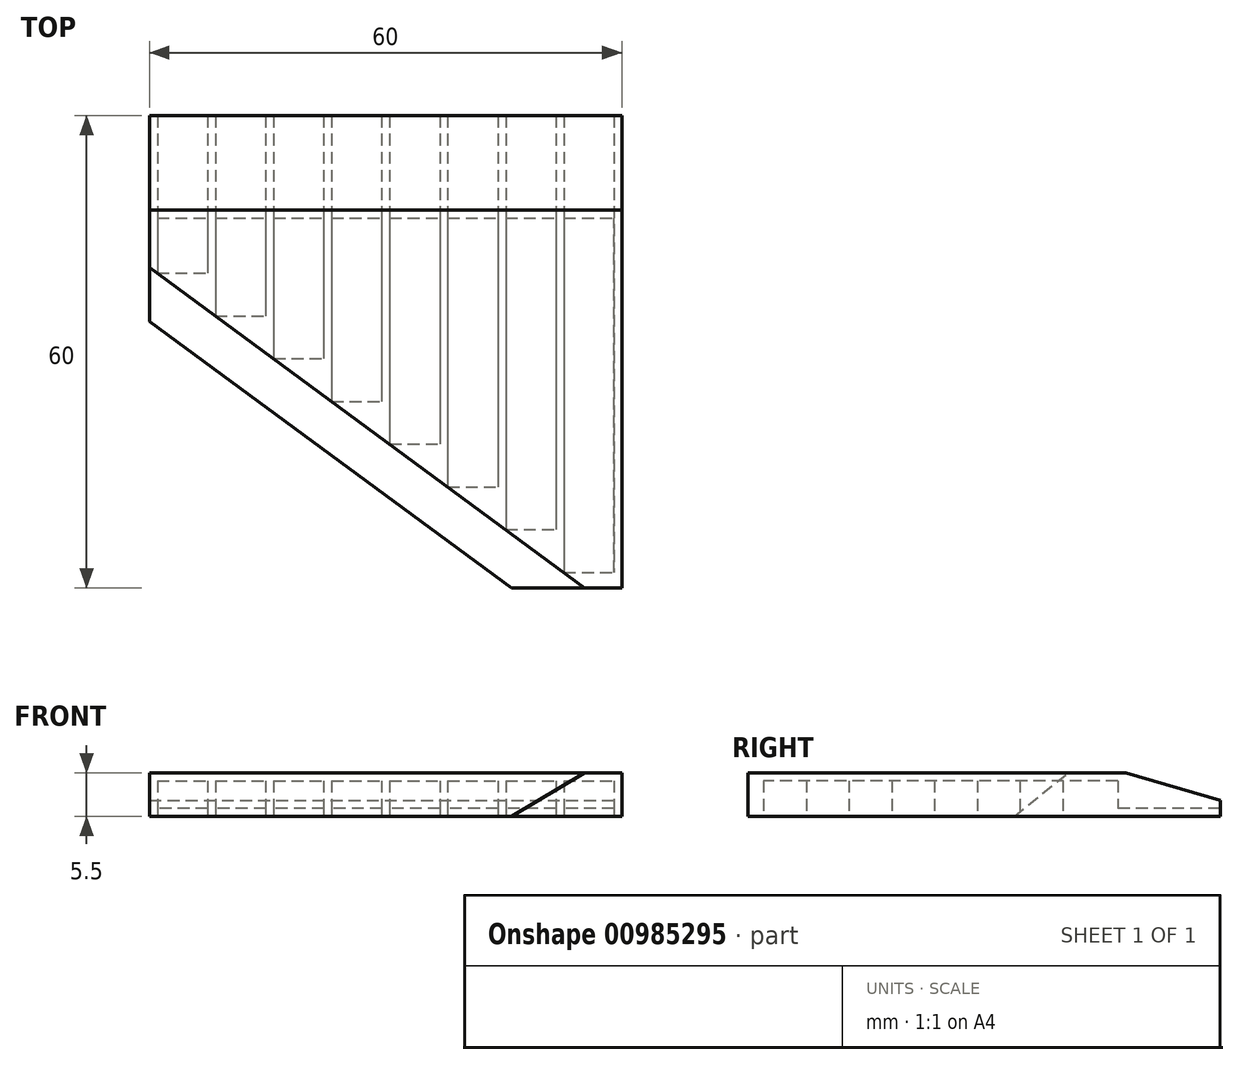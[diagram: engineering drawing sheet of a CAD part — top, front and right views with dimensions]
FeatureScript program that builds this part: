
annotation { "Feature Type Name" : "Feature", "Feature Type Description" : "" }
export const myFeature = defineFeature(function(context is Context, id is Id, definition is map)
    precondition{}
    {
        {
            var Q0;
            Q0=qCreatedBy(makeId("Top.planeOp"),FACE);
            var sketch = newSketch(context, id + "F0", { "sketchPlane" : qUnion([Q0])});
            skLineSegment(sketch, "E0.bottom", {"start": v(30, 30) * mm, "end": v(-30, 30) * mm});
            skLineSegment(sketch, "E0.top", {"start": v(30, -30) * mm, "end": v(-30, -30) * mm});
            skLineSegment(sketch, "E0.left", {"start": v(30, 30) * mm, "end": v(30, -30) * mm});
            skLineSegment(sketch, "E0.right", {"start": v(-30, 30) * mm, "end": v(-30, -30) * mm});
            skPoint(sketch, "E0.middle", {"position": v(0, 0) * mm});
            skSolve(sketch);
        }
        {
            var Q0;
            Q0=makeQuery(id+"F0.imprint","IMPRINT",FACE,{"disambiguationData":[TD([[makeQuery(id+"F0.imprint","IMPRINT",EDGE,{"derivedFrom":sQuery(id+"F0.wireOp",EDGE,"E0.bottom")}),1.0]])]});
            extrude(context, id + "F1", {"entities" : qUnion([Q0]), "depth" : 5.5 * mm, "offsetDistance" : 25 * mm});
        }
        {
            var Q0;
            Q0=makeQuery(id+"F1.opExtrude","SWEPT_FACE",FACE,{"disambiguationData":[OSD([sQuery(id+"F0.wireOp",EDGE,"E0.left")])]});
            var sketch = newSketch(context, id + "F2", { "sketchPlane" : qUnion([Q0])});
            skLineSegment(sketch, "E1", {"start": v(30, 2) * mm, "end": v(30, 5.5) * mm});
            skLineSegment(sketch, "E2", {"start": v(30, 5.5) * mm, "end": v(18, 5.5) * mm});
            skLineSegment(sketch, "E3", {"start": v(18, 5.5) * mm, "end": v(30, 2) * mm});
            skSolve(sketch);
        }
        {
            var Q0;
            Q0=qSketchRegion(id+"F2",true);
            var Q1;
            Q1=makeQuery(id+"F1.opExtrude","SWEPT_FACE",FACE,{"disambiguationData":[OSD([sQuery(id+"F0.wireOp",EDGE,"E0.right")])]});
            extrude(context, id + "F3", {"entities" : qUnion([Q0]), "operationType" : NewBodyOperationType.REMOVE, "endBound" : BoundingType.UP_TO_SURFACE, "oppositeDirection" : true, "depth" : 25 * mm, "endBoundEntityFace" : qUnion([Q1]), "offsetDistance" : 25 * mm});
        }
        {
            var Q0;
            Q0=makeQuery(id+"F1.opExtrude","CAP_FACE",FACE,{"disambiguationData":[OSD([sQuery(id+"F0.wireOp",EDGE,"E0.bottom"),sQuery(id+"F0.wireOp",EDGE,"E0.top"),sQuery(id+"F0.wireOp",EDGE,"E0.left"),sQuery(id+"F0.wireOp",EDGE,"E0.right")])],"isStart":true});
            var sketch = newSketch(context, id + "F4", { "sketchPlane" : qUnion([Q0])});
            skLineSegment(sketch, "E4", {"start": v(-29, -30) * mm, "end": v(29, -30) * mm});
            skLineSegment(sketch, "E5.bottom", {"start": v(-29, -30) * mm, "end": v(-22.62, -30) * mm});
            skLineSegment(sketch, "E5.top", {"start": v(-29, -17) * mm, "end": v(-22.62, -17) * mm});
            skLineSegment(sketch, "E5.left", {"start": v(-29, -30) * mm, "end": v(-29, -17) * mm});
            skLineSegment(sketch, "E5.right", {"start": v(-22.62, -30) * mm, "end": v(-22.62, -17) * mm});
            skLineSegment(sketch, "E6.bottom", {"start": v(-21.62, -30) * mm, "end": v(-15.25, -30) * mm});
            skLineSegment(sketch, "E6.top", {"start": v(-21.62, -17) * mm, "end": v(-15.25, -17) * mm});
            skLineSegment(sketch, "E6.left", {"start": v(-21.62, -30) * mm, "end": v(-21.62, -17) * mm});
            skLineSegment(sketch, "E6.right", {"start": v(-15.25, -30) * mm, "end": v(-15.25, -17) * mm});
            skLineSegment(sketch, "E7.bottom", {"start": v(-14.25, -30) * mm, "end": v(-7.87, -30) * mm});
            skLineSegment(sketch, "E7.top", {"start": v(-14.25, -17) * mm, "end": v(-7.87, -17) * mm});
            skLineSegment(sketch, "E7.left", {"start": v(-14.25, -30) * mm, "end": v(-14.25, -17) * mm});
            skLineSegment(sketch, "E7.right", {"start": v(-7.87, -30) * mm, "end": v(-7.87, -17) * mm});
            skLineSegment(sketch, "E8.bottom", {"start": v(-6.87, -30) * mm, "end": v(-0.5, -30) * mm});
            skLineSegment(sketch, "E8.top", {"start": v(-6.87, -17) * mm, "end": v(-0.5, -17) * mm});
            skLineSegment(sketch, "E8.left", {"start": v(-6.87, -30) * mm, "end": v(-6.87, -17) * mm});
            skLineSegment(sketch, "E8.right", {"start": v(-0.5, -30) * mm, "end": v(-0.5, -17) * mm});
            skLineSegment(sketch, "E9.bottom", {"start": v(0.5, -30) * mm, "end": v(6.88, -30) * mm});
            skLineSegment(sketch, "E9.top", {"start": v(0.5, -17) * mm, "end": v(6.88, -17) * mm});
            skLineSegment(sketch, "E9.left", {"start": v(0.5, -30) * mm, "end": v(0.5, -17) * mm});
            skLineSegment(sketch, "E9.right", {"start": v(6.88, -30) * mm, "end": v(6.88, -17) * mm});
            skLineSegment(sketch, "E10.bottom", {"start": v(7.88, -30) * mm, "end": v(14.25, -30) * mm});
            skLineSegment(sketch, "E10.top", {"start": v(7.88, -17) * mm, "end": v(14.25, -17) * mm});
            skLineSegment(sketch, "E10.left", {"start": v(7.88, -30) * mm, "end": v(7.88, -17) * mm});
            skLineSegment(sketch, "E10.right", {"start": v(14.25, -30) * mm, "end": v(14.25, -17) * mm});
            skLineSegment(sketch, "E11.bottom", {"start": v(15.25, -30) * mm, "end": v(21.63, -30) * mm});
            skLineSegment(sketch, "E11.top", {"start": v(15.25, -17) * mm, "end": v(21.63, -17) * mm});
            skLineSegment(sketch, "E11.left", {"start": v(15.25, -30) * mm, "end": v(15.25, -17) * mm});
            skLineSegment(sketch, "E11.right", {"start": v(21.63, -30) * mm, "end": v(21.63, -17) * mm});
            skLineSegment(sketch, "E12.bottom", {"start": v(22.63, -30) * mm, "end": v(29, -30) * mm});
            skLineSegment(sketch, "E12.top", {"start": v(22.62, -17) * mm, "end": v(29, -17) * mm});
            skLineSegment(sketch, "E12.left", {"start": v(22.63, -30) * mm, "end": v(22.63, -17) * mm});
            skLineSegment(sketch, "E12.right", {"start": v(29, -30) * mm, "end": v(29, -17) * mm});
            skLineSegment(sketch, "E13", {"start": v(-22.62, -30) * mm, "end": v(-21.62, -30) * mm, "construction": true});
            skLineSegment(sketch, "E14", {"start": v(-15.25, -30) * mm, "end": v(-14.25, -30) * mm, "construction": true});
            skLineSegment(sketch, "E15", {"start": v(-7.87, -30) * mm, "end": v(-6.87, -30) * mm, "construction": true});
            skLineSegment(sketch, "E16", {"start": v(-0.5, -30) * mm, "end": v(0.5, -30) * mm, "construction": true});
            skLineSegment(sketch, "E17", {"start": v(6.88, -30) * mm, "end": v(7.88, -30) * mm, "construction": true});
            skLineSegment(sketch, "E18", {"start": v(14.25, -30) * mm, "end": v(15.25, -30) * mm, "construction": true});
            skLineSegment(sketch, "E19", {"start": v(21.63, -30) * mm, "end": v(22.63, -30) * mm, "construction": true});
            skSolve(sketch);
        }
        {
            var Q0;
            {Q0=qUnion([makeQuery(id+"F4.imprint","IMPRINT",FACE,{"disambiguationData":[TD([[makeQuery(id+"F4.imprint","IMPRINT",EDGE,{"derivedFrom":sQuery(id+"F4.wireOp",EDGE,"E5.top")}),-1.0]])]}),makeQuery(id+"F4.imprint","IMPRINT",FACE,{"disambiguationData":[TD([[makeQuery(id+"F4.imprint","IMPRINT",EDGE,{"derivedFrom":sQuery(id+"F4.wireOp",EDGE,"E7.top")}),-1.0]])]}),makeQuery(id+"F4.imprint","IMPRINT",FACE,{"disambiguationData":[TD([[makeQuery(id+"F4.imprint","IMPRINT",EDGE,{"derivedFrom":sQuery(id+"F4.wireOp",EDGE,"E11.top")}),-1.0]])]}),makeQuery(id+"F4.imprint","IMPRINT",FACE,{"disambiguationData":[TD([[makeQuery(id+"F4.imprint","IMPRINT",EDGE,{"derivedFrom":sQuery(id+"F4.wireOp",EDGE,"E10.top")}),-1.0]])]}),makeQuery(id+"F4.imprint","IMPRINT",FACE,{"disambiguationData":[TD([[makeQuery(id+"F4.imprint","IMPRINT",EDGE,{"derivedFrom":sQuery(id+"F4.wireOp",EDGE,"E9.top")}),-1.0]])]}),makeQuery(id+"F4.imprint","IMPRINT",FACE,{"disambiguationData":[TD([[makeQuery(id+"F4.imprint","IMPRINT",EDGE,{"derivedFrom":sQuery(id+"F4.wireOp",EDGE,"E6.top")}),-1.0]])]}),makeQuery(id+"F4.imprint","IMPRINT",FACE,{"disambiguationData":[TD([[makeQuery(id+"F4.imprint","IMPRINT",EDGE,{"derivedFrom":sQuery(id+"F4.wireOp",EDGE,"E8.top")}),-1.0]])]}),makeQuery(id+"F4.imprint","IMPRINT",FACE,{"disambiguationData":[TD([[makeQuery(id+"F4.imprint","IMPRINT",EDGE,{"derivedFrom":sQuery(id+"F4.wireOp",EDGE,"E12.top")}),-1.0]])]})]);}
            extrude(context, id + "F5", {"entities" : qUnion([Q0]), "operationType" : NewBodyOperationType.REMOVE, "oppositeDirection" : true, "depth" : 1 * mm, "offsetDistance" : 25 * mm});
        }
        {
            var Q0;
            Q0=makeQuery(id+"F1.opExtrude","CAP_FACE",FACE,{"disambiguationData":[OSD([sQuery(id+"F0.wireOp",EDGE,"E0.bottom"),sQuery(id+"F0.wireOp",EDGE,"E0.top"),sQuery(id+"F0.wireOp",EDGE,"E0.left"),sQuery(id+"F0.wireOp",EDGE,"E0.right")])],"isStart":true});
            var sketch = newSketch(context, id + "F6", { "sketchPlane" : qUnion([Q0])});
            skLineSegment(sketch, "E20", {"start": v(29, -17) * mm, "end": v(22.62, -17) * mm});
            skLineSegment(sketch, "E21", {"start": v(-29, -17) * mm, "end": v(-29, -10) * mm});
            skLineSegment(sketch, "E22", {"start": v(29, 28) * mm, "end": v(29, -17) * mm});
            skLineSegment(sketch, "E23", {"start": v(-22.62, -17) * mm, "end": v(-22.62, -10) * mm});
            skLineSegment(sketch, "E24", {"start": v(-21.62, -17) * mm, "end": v(-21.62, -4.57) * mm});
            skLineSegment(sketch, "E25", {"start": v(-15.25, -17) * mm, "end": v(-15.25, -4.57) * mm});
            skLineSegment(sketch, "E26", {"start": v(-14.25, -17) * mm, "end": v(-14.25, 0.86) * mm});
            skLineSegment(sketch, "E27", {"start": v(-7.87, -17) * mm, "end": v(-7.88, 0.86) * mm});
            skLineSegment(sketch, "E28", {"start": v(-6.87, -17) * mm, "end": v(-6.87, 6.29) * mm});
            skLineSegment(sketch, "E29", {"start": v(-0.5, -17) * mm, "end": v(-0.5, 6.29) * mm});
            skLineSegment(sketch, "E30", {"start": v(0.5, -17) * mm, "end": v(0.5, 11.71) * mm});
            skLineSegment(sketch, "E31", {"start": v(6.88, -17) * mm, "end": v(6.88, 11.71) * mm});
            skLineSegment(sketch, "E32", {"start": v(7.88, -17) * mm, "end": v(7.88, 17.14) * mm});
            skLineSegment(sketch, "E33", {"start": v(14.25, -17) * mm, "end": v(14.25, 17.14) * mm});
            skLineSegment(sketch, "E34", {"start": v(15.25, -17) * mm, "end": v(15.25, 22.57) * mm});
            skLineSegment(sketch, "E35", {"start": v(21.63, -17) * mm, "end": v(21.63, 22.57) * mm});
            skLineSegment(sketch, "E36", {"start": v(22.62, -17) * mm, "end": v(22.62, 28) * mm});
            skLineSegment(sketch, "E37.trimOffspring", {"start": v(-22.62, -17) * mm, "end": v(-29, -17) * mm});
            skLineSegment(sketch, "E38.trimOffspring", {"start": v(-15.25, -17) * mm, "end": v(-21.62, -17) * mm});
            skLineSegment(sketch, "E39.trimOffspring", {"start": v(-7.87, -17) * mm, "end": v(-14.25, -17) * mm});
            skLineSegment(sketch, "E40.trimOffspring", {"start": v(-0.5, -17) * mm, "end": v(-6.87, -17) * mm});
            skLineSegment(sketch, "E41.trimOffspring", {"start": v(6.88, -17) * mm, "end": v(0.5, -17) * mm});
            skLineSegment(sketch, "E42.trimOffspring", {"start": v(14.25, -17) * mm, "end": v(7.88, -17) * mm});
            skLineSegment(sketch, "E43", {"start": v(-29, -10) * mm, "end": v(-22.62, -10) * mm});
            skLineSegment(sketch, "E44", {"start": v(-21.62, -4.57) * mm, "end": v(-15.25, -4.57) * mm});
            skLineSegment(sketch, "E45", {"start": v(-14.25, 0.86) * mm, "end": v(-7.88, 0.86) * mm});
            skLineSegment(sketch, "E46", {"start": v(-6.87, 6.29) * mm, "end": v(-0.5, 6.29) * mm});
            skLineSegment(sketch, "E47", {"start": v(0.5, 11.71) * mm, "end": v(6.88, 11.71) * mm});
            skLineSegment(sketch, "E48", {"start": v(7.88, 17.14) * mm, "end": v(14.25, 17.14) * mm});
            skLineSegment(sketch, "E49", {"start": v(15.25, 22.57) * mm, "end": v(21.63, 22.57) * mm});
            skLineSegment(sketch, "E50", {"start": v(22.62, 28) * mm, "end": v(29, 28) * mm});
            skLineSegment(sketch, "E51", {"start": v(-29, -10) * mm, "end": v(-21.62, -4.57) * mm, "construction": true});
            skLineSegment(sketch, "E52", {"start": v(-21.62, -4.57) * mm, "end": v(-14.25, 0.86) * mm, "construction": true});
            skLineSegment(sketch, "E53", {"start": v(-14.25, 0.86) * mm, "end": v(-6.87, 6.29) * mm, "construction": true});
            skLineSegment(sketch, "E54", {"start": v(-6.87, 6.29) * mm, "end": v(0.5, 11.71) * mm, "construction": true});
            skLineSegment(sketch, "E55", {"start": v(0.5, 11.71) * mm, "end": v(7.88, 17.14) * mm, "construction": true});
            skLineSegment(sketch, "E56", {"start": v(7.88, 17.14) * mm, "end": v(15.25, 22.57) * mm, "construction": true});
            skLineSegment(sketch, "E57", {"start": v(15.25, 22.57) * mm, "end": v(22.62, 28) * mm, "construction": true});
            skSolve(sketch);
        }
        {
            var Q0;
            Q0 = qSketchRegion(id + "F6", true);
            var Q1;
            Q1=makeQuery(id+"F6.imprint","IMPRINT",FACE,{"disambiguationData":[TD([[makeQuery(id+"F6.imprint","IMPRINT",EDGE,{"derivedFrom":sQuery(id+"F6.wireOp",EDGE,"E34")}),-1.0]])]});
            extrude(context, id + "F7", {"entities" : qUnion([Q0, Q1]), "operationType" : NewBodyOperationType.REMOVE, "oppositeDirection" : true, "depth" : 4.5 * mm, "offsetDistance" : 25 * mm});
        }
        {
            var Q0;
            Q0=makeQuery(id+"F1.opExtrude","CAP_FACE",FACE,{"disambiguationData":[OSD([sQuery(id+"F0.wireOp",EDGE,"E0.bottom"),sQuery(id+"F0.wireOp",EDGE,"E0.top"),sQuery(id+"F0.wireOp",EDGE,"E0.left"),sQuery(id+"F0.wireOp",EDGE,"E0.right")])],"isStart":true});
            var sketch = newSketch(context, id + "F8", { "sketchPlane" : qUnion([Q0])});
            skLineSegment(sketch, "E58", {"start": v(-30, -3.86) * mm, "end": v(16, 30) * mm});
            skLineSegment(sketch, "E59", {"start": v(-29, -10) * mm, "end": v(22.62, 28) * mm, "construction": true});
            skSolve(sketch);
        }
        {
            var Q0;
            {var subQ0=sQuery(id+"F8.wireOp",EDGE,"E58");Q0=makeQuery(id+"F8.imprint","IMPRINT",FACE,{"disambiguationData":[TD([[makeQuery(id+"F8.imprint","IMPRINT",EDGE,{"derivedFrom":subQ0}),1.0]])]});}
            var Q1;
            Q1=makeQuery(id+"F1.opExtrude","CAP_FACE",FACE,{"disambiguationData":[OSD([sQuery(id+"F0.wireOp",EDGE,"E0.bottom"),sQuery(id+"F0.wireOp",EDGE,"E0.top"),sQuery(id+"F0.wireOp",EDGE,"E0.left"),sQuery(id+"F0.wireOp",EDGE,"E0.right")])],"isStart":false});
            extrude(context, id + "F9", {"entities" : qUnion([Q0]), "operationType" : NewBodyOperationType.REMOVE, "endBound" : BoundingType.UP_TO_SURFACE, "oppositeDirection" : true, "depth" : 25 * mm, "endBoundEntityFace" : qUnion([Q1]), "offsetDistance" : 25 * mm, "hasDraft" : true, "draftAngle" : 45 * degree});
        }
    });
